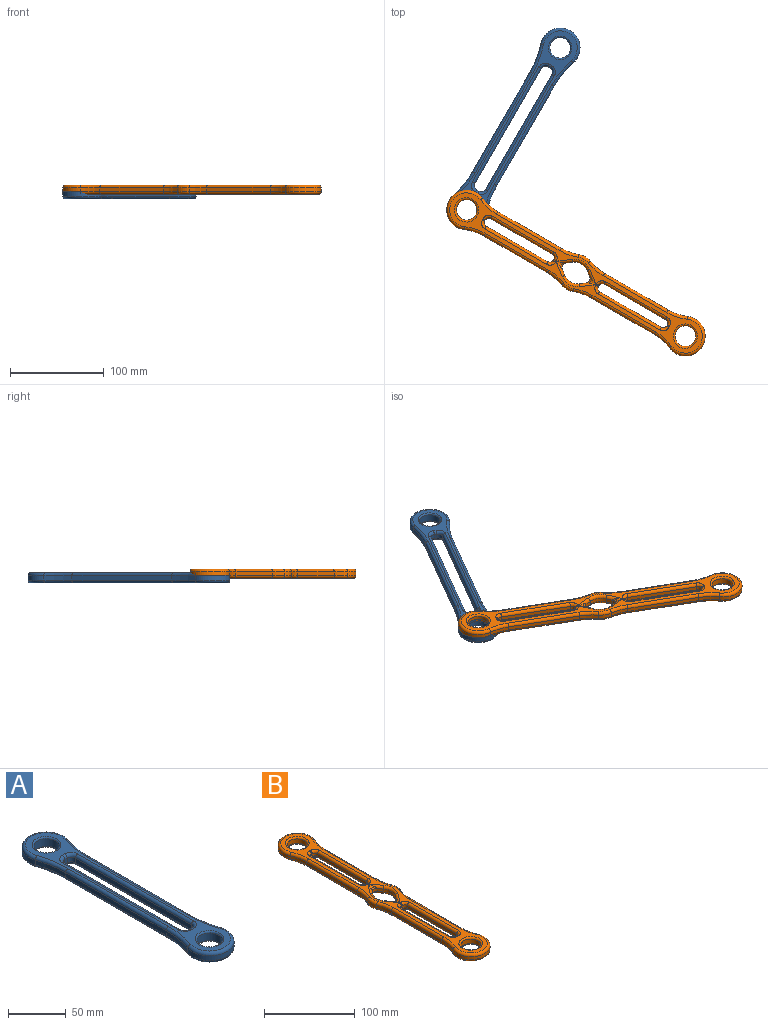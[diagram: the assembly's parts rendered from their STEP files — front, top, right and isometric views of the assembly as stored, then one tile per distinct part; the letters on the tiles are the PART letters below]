
ASSEMBLY  parts=2 mates=1
PART A: 56 faces, bbox 45.9x245.9x11 mm
  f0: cylinder r=5mm len=5mm, axis (0,0,-1), area 39.3mm2, adj f1,f11,f38,f50
  f1: plane 5x3mm, normal (0,1,0), area 15mm2, adj f0,f2,f40,f48
  f2: cylinder r=5mm len=5mm, axis (0,0,-1), area 39.3mm2, adj f1,f3,f42,f46
  f3: plane 142.03x5mm, normal (1,0,0), area 710.2mm2, adj f2,f4,f43,f44
  f4: cylinder r=5mm len=5mm, axis (0,0,-1), area 39.3mm2, adj f3,f5,f41,f45
  f5: plane 5x3mm, normal (0,-1,0), area 15mm2, adj f4,f6,f39,f47
  f6: cylinder r=5mm len=5mm, axis (0,0,-1), area 39.3mm2, adj f5,f11,f37,f49
  f7: plane 123.38x5mm, normal (1,0,0), area 616.9mm2, adj f18,f19,f20,f35
  f8: cylinder r=21.21mm len=42.43mm, axis (0,0,-1), area 401.4mm2, adj f16,f19,f24,f32
  f9: plane 123.38x5mm, normal (-1,0,0), area 616.9mm2, adj f16,f17,f27,f28
  f10: cylinder r=11mm len=22mm, axis (0,0,-1), area 552.9mm2, adj f53,f55
  f11: plane 142.03x5mm, normal (-1,0,0), area 710.2mm2, adj f0,f6,f36,f51
  f12: cylinder r=21.21mm len=42.43mm, axis (0,0,-1), area 401.4mm2, adj f17,f18,f23,f31
  f13: cylinder r=11mm len=22mm, axis (0,0,-1), area 552.9mm2, adj f52,f54
  f14: plane 236.43x36.43mm, normal (0,0,1), area 2275.4mm2, adj f28,f29,f30,f31,f32,f33,f34,f35
  f15: plane 236.43x36.43mm, normal (0,0,-1), area 2275.4mm2, adj f20,f21,f22,f23,f24,f25,f26,f27
  f16: cylinder r=100mm len=31.61mm, axis (0,0,-1), area 160.8mm2, adj f8,f9,f26,f30
  f17: cylinder r=100mm len=31.61mm, axis (0,0,-1), area 160.8mm2, adj f9,f12,f25,f29
  f18: cylinder r=100mm len=31.61mm, axis (0,0,-1), area 160.8mm2, adj f7,f12,f21,f33
  f19: cylinder r=100mm len=31.61mm, axis (0,0,-1), area 160.8mm2, adj f7,f8,f22,f34
  f20: cylinder r=3mm len=123.38mm, axis (0,1,0), area 581.4mm2, adj f7,f15,f21,f22
  f21: torus R=103mm, axis (0,0,1), area 153.2mm2, adj f15,f18,f20,f23
  f22: torus R=103mm, axis (0,0,1), area 153.2mm2, adj f15,f19,f20,f24
  f23: torus R=18.21mm, axis (0,0,1), area 358.9mm2, adj f12,f15,f21,f25
  f24: torus R=18.21mm, axis (0,0,1), area 358.9mm2, adj f8,f15,f22,f26
  f25: torus R=103mm, axis (0,0,1), area 153.2mm2, adj f15,f17,f23,f27
  f26: torus R=103mm, axis (0,0,1), area 153.2mm2, adj f15,f16,f24,f27
  f27: cylinder r=3mm len=123.38mm, axis (0,-1,0), area 581.4mm2, adj f9,f15,f25,f26
  f28: cylinder r=3mm len=123.38mm, axis (0,1,0), area 581.4mm2, adj f9,f14,f29,f30
  f29: torus R=103mm, axis (0,0,1), area 153.2mm2, adj f14,f17,f28,f31
  f30: torus R=103mm, axis (0,0,1), area 153.2mm2, adj f14,f16,f28,f32
  f31: torus R=18.21mm, axis (0,0,1), area 358.9mm2, adj f12,f14,f29,f33
  f32: torus R=18.21mm, axis (0,0,1), area 358.9mm2, adj f8,f14,f30,f34
  f33: torus R=103mm, axis (0,0,1), area 153.2mm2, adj f14,f18,f31,f35
  f34: torus R=103mm, axis (0,0,1), area 153.2mm2, adj f14,f19,f32,f35
  f35: cylinder r=3mm len=123.38mm, axis (0,-1,0), area 581.4mm2, adj f7,f14,f33,f34
  f36: cylinder r=3mm len=142.03mm, axis (0,-1,0), area 669.3mm2, adj f11,f15,f37,f38
  f37: torus R=8mm, axis (0,0,1), area 45.1mm2, adj f6,f15,f36,f39
  f38: torus R=8mm, axis (0,0,1), area 45.1mm2, adj f0,f15,f36,f40
  f39: cylinder r=3mm len=3mm, axis (1,0,0), area 14.1mm2, adj f5,f15,f37,f41
  f40: cylinder r=3mm len=3mm, axis (-1,0,0), area 14.1mm2, adj f1,f15,f38,f42
  f41: torus R=8mm, axis (0,0,1), area 45.1mm2, adj f4,f15,f39,f43
  f42: torus R=8mm, axis (0,0,1), area 45.1mm2, adj f2,f15,f40,f43
  f43: cylinder r=3mm len=142.03mm, axis (0,1,0), area 669.3mm2, adj f3,f15,f41,f42
  f44: cylinder r=3mm len=142.03mm, axis (0,-1,0), area 669.3mm2, adj f3,f14,f45,f46
  f45: torus R=8mm, axis (0,0,1), area 45.1mm2, adj f4,f14,f44,f47
  f46: torus R=8mm, axis (0,0,1), area 45.1mm2, adj f2,f14,f44,f48
  f47: cylinder r=3mm len=3mm, axis (-1,0,0), area 14.1mm2, adj f5,f14,f45,f49
  f48: cylinder r=3mm len=3mm, axis (1,0,0), area 14.1mm2, adj f1,f14,f46,f50
  f49: torus R=8mm, axis (0,0,1), area 45.1mm2, adj f6,f14,f47,f51
  f50: torus R=8mm, axis (0,0,1), area 45.1mm2, adj f0,f14,f48,f51
  f51: cylinder r=3mm len=142.03mm, axis (0,1,0), area 669.3mm2, adj f11,f14,f49,f50
  f52: torus R=12.5mm, axis (0,0,1), area 170.9mm2, adj f13,f15
  f53: torus R=12.5mm, axis (0,0,1), area 170.9mm2, adj f10,f15
  f54: torus R=12.5mm, axis (0,0,1), area 170.9mm2, adj f13,f14
  f55: torus R=12.5mm, axis (0,0,1), area 170.9mm2, adj f10,f14
PART B: 132 faces, bbox 45.9x315.9x10 mm
  f0: bspline ~7.76x6.01mm, area 20.7mm2, adj f92,f93,f95,f125
  f1: bspline ~7.76x6.01mm, area 20.7mm2, adj f113,f114,f117,f127
  f2: bspline ~7.76x6.01mm, area 20.7mm2, adj f85,f86,f87,f122
  f3: bspline ~7.76x6.01mm, area 20.7mm2, adj f107,f108,f109,f124
  f4: cylinder r=4mm len=4mm, axis (0,0,-1), area 25.1mm2, adj f5,f31,f94,f116
  f5: plane 4x1.46mm, normal (0,1,0), area 5.8mm2, adj f4,f6,f96,f118
  f6: cylinder r=4mm len=4mm, axis (0,0,-1), area 25.1mm2, adj f5,f7,f98,f120
  f7: plane 76.33x4mm, normal (1,0,0), area 305.3mm2, adj f6,f8,f99,f121
  f8: cylinder r=4mm len=4mm, axis (0,0,-1), area 25.1mm2, adj f7,f9,f97,f119
  f9: plane 4x1.46mm, normal (0,-1,0), area 5.8mm2, adj f8,f10,f95,f117
  f10: cylinder r=4mm len=4mm, axis (0,0,-1), area 25.1mm2, adj f9,f31,f91,f115
  f11: cylinder r=4mm len=4mm, axis (0,0,-1), area 25.1mm2, adj f12,f32,f83,f106
  f12: plane 4x1.46mm, normal (0,1,0), area 5.8mm2, adj f11,f13,f85,f107
  f13: cylinder r=4mm len=4mm, axis (0,0,-1), area 25.1mm2, adj f12,f14,f84,f105
  f14: plane 76.33x4mm, normal (1,0,0), area 305.3mm2, adj f13,f15,f82,f103
  f15: cylinder r=4mm len=4mm, axis (0,0,-1), area 25.1mm2, adj f14,f16,f80,f101
  f16: plane 4x1.46mm, normal (0,-1,0), area 5.8mm2, adj f15,f17,f78,f100
  f17: cylinder r=4mm len=4mm, axis (0,0,-1), area 25.1mm2, adj f16,f32,f79,f102
  f18: plane 5.67x4.25mm, normal (0.8,-0.6,0), area 28.3mm2, adj f33,f87,f108,f123
  f19: plane 5.67x4.25mm, normal (-0.8,-0.6,0), area 28.3mm2, adj f20,f86,f109,f123
  f20: cylinder r=15mm len=18mm, axis (0,0,-1), area 77.2mm2, adj f19,f21,f88,f111
  f21: plane 5.67x4.25mm, normal (-0.8,0.6,0), area 28.3mm2, adj f20,f92,f114,f126
  f22: plane 5.67x4.25mm, normal (0.8,0.6,0), area 28.3mm2, adj f33,f93,f113,f126
  f23: cylinder r=21.21mm len=42.43mm, axis (0,0,-1), area 336.2mm2, adj f38,f39,f58,f66
  f24: plane 78.49x4mm, normal (1,0,0), area 314mm2, adj f39,f45,f54,f70
  f25: cylinder r=20mm len=14.49mm, axis (0,0,-1), area 59.3mm2, adj f44,f45,f50,f74
  f26: plane 78.49x4mm, normal (1,0,0), area 314mm2, adj f41,f44,f46,f77
  f27: cylinder r=21.21mm len=42.43mm, axis (0,0,-1), area 336.2mm2, adj f40,f41,f49,f73
  f28: plane 78.49x4mm, normal (-1,0,0), area 314mm2, adj f40,f42,f53,f69
  f29: cylinder r=20mm len=14.49mm, axis (0,0,-1), area 59.3mm2, adj f42,f43,f57,f65
  f30: cylinder r=11mm len=22mm, axis (0,0,-1), area 414.7mm2, adj f128,f130
  f31: plane 76.33x4mm, normal (-1,0,0), area 305.3mm2, adj f4,f10,f90,f112
  f32: plane 76.33x4mm, normal (-1,0,0), area 305.3mm2, adj f11,f17,f81,f104
  f33: cylinder r=15mm len=18mm, axis (0,0,-1), area 77.2mm2, adj f18,f22,f89,f110
  f34: plane 78.49x4mm, normal (-1,0,0), area 314mm2, adj f38,f43,f61,f62
  f35: cylinder r=11mm len=22mm, axis (0,0,-1), area 414.7mm2, adj f129,f131
  f36: plane 306.43x36.43mm, normal (0,0,1), area 3405.9mm2, adj f62,f63,f64,f65,f66,f67,f68,f69
  f37: plane 306.43x36.43mm, normal (0,0,-1), area 3405.9mm2, adj f46,f47,f48,f49,f50,f51,f52,f53
  f38: cylinder r=53.59mm len=21.38mm, axis (0,0,-1), area 88mm2, adj f23,f34,f60,f64
  f39: cylinder r=53.59mm len=21.38mm, axis (0,0,-1), area 88mm2, adj f23,f24,f56,f68
  f40: cylinder r=53.59mm len=21.38mm, axis (0,0,-1), area 88mm2, adj f27,f28,f51,f71
  f41: cylinder r=53.59mm len=21.38mm, axis (0,0,-1), area 88mm2, adj f26,f27,f47,f75
  f42: cylinder r=53.59mm len=19.42mm, axis (0,0,-1), area 79.5mm2, adj f28,f29,f55,f67
  f43: cylinder r=53.59mm len=19.42mm, axis (0,0,-1), area 79.5mm2, adj f29,f34,f59,f63
  f44: cylinder r=53.59mm len=19.42mm, axis (0,0,-1), area 79.5mm2, adj f25,f26,f48,f76
  f45: cylinder r=53.59mm len=19.42mm, axis (0,0,-1), area 79.5mm2, adj f24,f25,f52,f72
  f46: cylinder r=3mm len=78.49mm, axis (0,1,0), area 369.9mm2, adj f26,f37,f47,f48
  f47: torus R=56.59mm, axis (0,0,1), area 105.8mm2, adj f37,f41,f46,f49
  f48: torus R=56.59mm, axis (0,0,1), area 95.5mm2, adj f37,f44,f46,f50
  f49: torus R=18.21mm, axis (0,0,1), area 375.8mm2, adj f27,f37,f47,f51
  f50: torus R=17mm, axis (0,0,1), area 66.1mm2, adj f25,f37,f48,f52
  f51: torus R=56.59mm, axis (0,0,1), area 105.8mm2, adj f37,f40,f49,f53
  f52: torus R=56.59mm, axis (0,0,1), area 95.5mm2, adj f37,f45,f50,f54
  f53: cylinder r=3mm len=78.49mm, axis (0,-1,0), area 369.9mm2, adj f28,f37,f51,f55
  f54: cylinder r=3mm len=78.49mm, axis (0,1,0), area 369.9mm2, adj f24,f37,f52,f56
  f55: torus R=56.59mm, axis (0,0,1), area 95.5mm2, adj f37,f42,f53,f57
  f56: torus R=56.59mm, axis (0,0,1), area 105.8mm2, adj f37,f39,f54,f58
  f57: torus R=17mm, axis (0,0,1), area 66.1mm2, adj f29,f37,f55,f59
  f58: torus R=18.21mm, axis (0,0,1), area 375.8mm2, adj f23,f37,f56,f60
  f59: torus R=56.59mm, axis (0,0,1), area 95.5mm2, adj f37,f43,f57,f61
  f60: torus R=56.59mm, axis (0,0,1), area 105.8mm2, adj f37,f38,f58,f61
  f61: cylinder r=3mm len=78.49mm, axis (0,-1,0), area 369.9mm2, adj f34,f37,f59,f60
  f62: cylinder r=3mm len=78.49mm, axis (0,1,0), area 369.9mm2, adj f34,f36,f63,f64
  f63: torus R=56.59mm, axis (0,0,1), area 95.5mm2, adj f36,f43,f62,f65
  f64: torus R=56.59mm, axis (0,0,1), area 105.8mm2, adj f36,f38,f62,f66
  f65: torus R=17mm, axis (0,0,1), area 66.1mm2, adj f29,f36,f63,f67
  f66: torus R=18.21mm, axis (0,0,1), area 375.8mm2, adj f23,f36,f64,f68
  f67: torus R=56.59mm, axis (0,0,1), area 95.5mm2, adj f36,f42,f65,f69
  f68: torus R=56.59mm, axis (0,0,1), area 105.8mm2, adj f36,f39,f66,f70
  f69: cylinder r=3mm len=78.49mm, axis (0,1,0), area 369.9mm2, adj f28,f36,f67,f71
  f70: cylinder r=3mm len=78.49mm, axis (0,-1,0), area 369.9mm2, adj f24,f36,f68,f72
  f71: torus R=56.59mm, axis (0,0,1), area 105.8mm2, adj f36,f40,f69,f73
  f72: torus R=56.59mm, axis (0,0,1), area 95.5mm2, adj f36,f45,f70,f74
  f73: torus R=18.21mm, axis (0,0,1), area 375.8mm2, adj f27,f36,f71,f75
  f74: torus R=17mm, axis (0,0,1), area 66.1mm2, adj f25,f36,f72,f76
  f75: torus R=56.59mm, axis (0,0,1), area 105.8mm2, adj f36,f41,f73,f77
  f76: torus R=56.59mm, axis (0,0,1), area 95.5mm2, adj f36,f44,f74,f77
  f77: cylinder r=3mm len=78.49mm, axis (0,-1,0), area 369.9mm2, adj f26,f36,f75,f76
  f78: cylinder r=3mm len=3mm, axis (1,0,0), area 6.9mm2, adj f16,f37,f79,f80
  f79: torus R=7mm, axis (0,0,1), area 37.7mm2, adj f17,f37,f78,f81
  f80: torus R=7mm, axis (0,0,1), area 37.7mm2, adj f15,f37,f78,f82
  f81: cylinder r=3mm len=76.33mm, axis (0,-1,0), area 359.7mm2, adj f32,f37,f79,f83
  f82: cylinder r=3mm len=76.33mm, axis (0,1,0), area 359.7mm2, adj f14,f37,f80,f84
  f83: torus R=7mm, axis (0,0,1), area 37.7mm2, adj f11,f37,f81,f85
  f84: torus R=7mm, axis (0,0,1), area 37.7mm2, adj f13,f37,f82,f85
  f85: cylinder r=3mm len=3mm, axis (-1,0,0), area 6.9mm2, adj f2,f12,f37,f83,f84,f86,f87
  f86: cylinder r=3mm len=15.89mm, axis (0.6,-0.8,0), area 51.6mm2, adj f2,f19,f37,f85,f88,f122
  f87: cylinder r=3mm len=15.89mm, axis (0.6,0.8,0), area 51.6mm2, adj f2,f18,f37,f85,f89,f122
  f88: torus R=18mm, axis (0,0,1), area 97.6mm2, adj f20,f37,f86,f92
  f89: torus R=18mm, axis (0,0,1), area 97.6mm2, adj f33,f37,f87,f93
  f90: cylinder r=3mm len=76.33mm, axis (0,-1,0), area 359.7mm2, adj f31,f37,f91,f94
  f91: torus R=7mm, axis (0,0,1), area 37.7mm2, adj f10,f37,f90,f95
  f92: cylinder r=3mm len=15.89mm, axis (-0.6,-0.8,0), area 51.6mm2, adj f0,f21,f37,f88,f95,f125
  f93: cylinder r=3mm len=15.89mm, axis (-0.6,0.8,0), area 51.6mm2, adj f0,f22,f37,f89,f95,f125
  f94: torus R=7mm, axis (0,0,1), area 37.7mm2, adj f4,f37,f90,f96
  f95: cylinder r=3mm len=3mm, axis (1,0,0), area 6.9mm2, adj f0,f9,f37,f91,f92,f93,f97
  f96: cylinder r=3mm len=3mm, axis (-1,0,0), area 6.9mm2, adj f5,f37,f94,f98
  f97: torus R=7mm, axis (0,0,1), area 37.7mm2, adj f8,f37,f95,f99
  f98: torus R=7mm, axis (0,0,1), area 37.7mm2, adj f6,f37,f96,f99
  f99: cylinder r=3mm len=76.33mm, axis (0,1,0), area 359.7mm2, adj f7,f37,f97,f98
  f100: cylinder r=3mm len=3mm, axis (-1,0,0), area 6.9mm2, adj f16,f36,f101,f102
  f101: torus R=7mm, axis (0,0,1), area 37.7mm2, adj f15,f36,f100,f103
  f102: torus R=7mm, axis (0,0,1), area 37.7mm2, adj f17,f36,f100,f104
  f103: cylinder r=3mm len=76.33mm, axis (0,-1,0), area 359.7mm2, adj f14,f36,f101,f105
  f104: cylinder r=3mm len=76.33mm, axis (0,1,0), area 359.7mm2, adj f32,f36,f102,f106
  f105: torus R=7mm, axis (0,0,1), area 37.7mm2, adj f13,f36,f103,f107
  f106: torus R=7mm, axis (0,0,1), area 37.7mm2, adj f11,f36,f104,f107
  f107: cylinder r=3mm len=3mm, axis (1,0,0), area 6.9mm2, adj f3,f12,f36,f105,f106,f108,f109
  f108: cylinder r=3mm len=15.89mm, axis (-0.6,-0.8,0), area 51.6mm2, adj f3,f18,f36,f107,f110,f124
  f109: cylinder r=3mm len=15.89mm, axis (-0.6,0.8,0), area 51.6mm2, adj f3,f19,f36,f107,f111,f124
  f110: torus R=18mm, axis (0,0,1), area 97.6mm2, adj f33,f36,f108,f113
  f111: torus R=18mm, axis (0,0,1), area 97.6mm2, adj f20,f36,f109,f114
  f112: cylinder r=3mm len=76.33mm, axis (0,1,0), area 359.7mm2, adj f31,f36,f115,f116
  f113: cylinder r=3mm len=15.89mm, axis (0.6,-0.8,0), area 51.6mm2, adj f1,f22,f36,f110,f117,f127
  f114: cylinder r=3mm len=15.89mm, axis (0.6,0.8,0), area 51.6mm2, adj f1,f21,f36,f111,f117,f127
  f115: torus R=7mm, axis (0,0,1), area 37.7mm2, adj f10,f36,f112,f117
  f116: torus R=7mm, axis (0,0,1), area 37.7mm2, adj f4,f36,f112,f118
  f117: cylinder r=3mm len=3mm, axis (-1,0,0), area 6.9mm2, adj f1,f9,f36,f113,f114,f115,f119
  f118: cylinder r=3mm len=3mm, axis (1,0,0), area 6.9mm2, adj f5,f36,f116,f120
  f119: torus R=7mm, axis (0,0,1), area 37.7mm2, adj f8,f36,f117,f121
  f120: torus R=7mm, axis (0,0,1), area 37.7mm2, adj f6,f36,f118,f121
  f121: cylinder r=3mm len=76.33mm, axis (0,-1,0), area 359.7mm2, adj f7,f36,f119,f120
  f122: bspline ~8x5.33mm, area 19.8mm2, adj f2,f86,f87,f123
  f123: cylinder r=5mm len=8mm, axis (0,0,1), area 37.1mm2, adj f18,f19,f122,f124
  f124: bspline ~8x5.33mm, area 19.8mm2, adj f3,f108,f109,f123
  f125: bspline ~8x5.33mm, area 19.8mm2, adj f0,f92,f93,f126
  f126: cylinder r=5mm len=8mm, axis (0,0,1), area 37.1mm2, adj f21,f22,f125,f127
  f127: bspline ~8x5.33mm, area 19.8mm2, adj f1,f113,f114,f126
  f128: torus R=13mm, axis (0,0,1), area 231.5mm2, adj f30,f37
  f129: torus R=13mm, axis (0,0,1), area 231.5mm2, adj f35,f37
  f130: torus R=13mm, axis (0,0,1), area 231.5mm2, adj f30,f36
  f131: torus R=13mm, axis (0,0,1), area 231.5mm2, adj f35,f36
PLACE A rot(axis=(0,0,-1),30deg) t=(135.7,-55.7,42.72)mm
PLACE B rot(axis=(0,0,1),60deg) t=(65.21,-147.79,47.64)mm
MATE revolute A.f10 <-> B.f27  axis (0,0,-1) through (85.7,-142.3,48.22)mm
